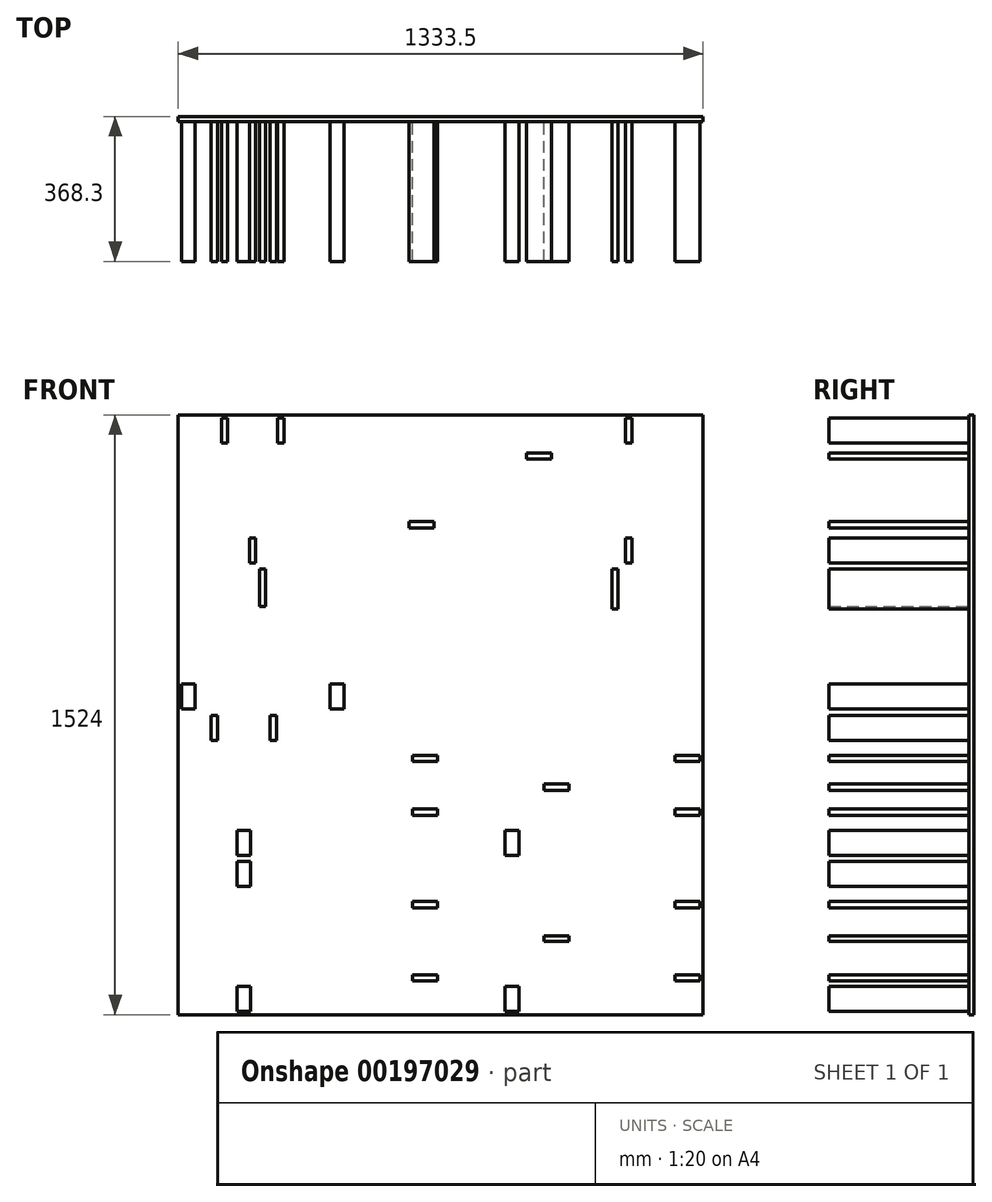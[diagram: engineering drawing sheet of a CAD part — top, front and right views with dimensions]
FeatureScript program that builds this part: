
annotation { "Feature Type Name" : "Feature", "Feature Type Description" : "" }
export const myFeature = defineFeature(function(context is Context, id is Id, definition is map)
    precondition{}
    {
        {
            var Q0;
            Q0=qCreatedBy(makeId("Front.planeOp"),FACE);
            var sketch = newSketch(context, id + "F0", { "sketchPlane" : qUnion([Q0])});
            skLineSegment(sketch, "E0.bottom", {"start": v(0, 0) * mm, "end": v(1333.5, 0) * mm});
            skLineSegment(sketch, "E0.top", {"start": v(0, 1524) * mm, "end": v(1333.5, 1524) * mm});
            skLineSegment(sketch, "E0.left", {"start": v(0, 0) * mm, "end": v(0, 1524) * mm});
            skLineSegment(sketch, "E0.right", {"start": v(1333.5, 0) * mm, "end": v(1333.5, 1524) * mm});
            skLineSegment(sketch, "E1.bottom", {"start": v(0, 1147.76) * mm, "end": v(1333.5, 1147.76) * mm, "construction": true});
            skLineSegment(sketch, "E1.top", {"start": v(0, 1131.89) * mm, "end": v(1333.5, 1131.89) * mm, "construction": true});
            skLineSegment(sketch, "E2.bottom", {"start": v(0, 776.29) * mm, "end": v(1333.5, 776.29) * mm, "construction": true});
            skLineSegment(sketch, "E2.top", {"start": v(0, 760.41) * mm, "end": v(1333.5, 760.41) * mm, "construction": true});
            skLineSegment(sketch, "E3.bottom", {"start": v(0, 404.81) * mm, "end": v(1333.5, 404.81) * mm, "construction": true});
            skLineSegment(sketch, "E3.top", {"start": v(0, 388.94) * mm, "end": v(1333.5, 388.94) * mm, "construction": true});
            skLineSegment(sketch, "E4.left", {"start": v(325.44, 776.29) * mm, "end": v(325.44, 0) * mm, "construction": true});
            skLineSegment(sketch, "E5.trimOffspring", {"start": v(341.31, 776.29) * mm, "end": v(341.31, 0) * mm, "construction": true});
            skLineSegment(sketch, "E6.trimOffspring", {"start": v(658.81, 776.29) * mm, "end": v(658.81, 0) * mm, "construction": true});
            skLineSegment(sketch, "E7.trimOffspring", {"start": v(674.69, 776.29) * mm, "end": v(674.69, 0) * mm, "construction": true});
            skLineSegment(sketch, "E8.trimOffspring", {"start": v(992.19, 776.29) * mm, "end": v(992.19, 0) * mm, "construction": true});
            skLineSegment(sketch, "E9.trimOffspring", {"start": v(1008.06, 776.29) * mm, "end": v(1008.06, 0) * mm, "construction": true});
            skLineSegment(sketch, "E10.bottom", {"start": v(7.94, 1516.06) * mm, "end": v(1325.56, 1516.06) * mm, "construction": true});
            skLineSegment(sketch, "E10.top", {"start": v(7.94, 7.94) * mm, "end": v(1325.56, 7.94) * mm, "construction": true});
            skLineSegment(sketch, "E10.left", {"start": v(7.94, 1516.06) * mm, "end": v(7.94, 7.94) * mm, "construction": true});
            skLineSegment(sketch, "E10.right", {"start": v(1325.56, 1516.06) * mm, "end": v(1325.56, 7.94) * mm, "construction": true});
            skLineSegment(sketch, "E11.bottom", {"start": v(595.31, 658.81) * mm, "end": v(658.81, 658.81) * mm});
            skLineSegment(sketch, "E11.top", {"start": v(595.31, 642.94) * mm, "end": v(658.81, 642.94) * mm});
            skLineSegment(sketch, "E11.left", {"start": v(595.31, 658.81) * mm, "end": v(595.31, 642.94) * mm});
            skLineSegment(sketch, "E11.right", {"start": v(658.81, 658.81) * mm, "end": v(658.81, 642.94) * mm});
            skLineSegment(sketch, "E12.bottom", {"start": v(896.94, 1131.89) * mm, "end": v(912.81, 1131.89) * mm});
            skLineSegment(sketch, "E12.top", {"start": v(896.94, 776.29) * mm, "end": v(912.81, 776.29) * mm});
            skLineSegment(sketch, "E12.left", {"start": v(896.94, 1131.89) * mm, "end": v(896.94, 776.29) * mm, "construction": true});
            skLineSegment(sketch, "E12.right", {"start": v(912.81, 1131.89) * mm, "end": v(912.81, 776.29) * mm, "construction": true});
            skLineSegment(sketch, "E13.bottom", {"start": v(436.56, 1131.89) * mm, "end": v(420.69, 1131.89) * mm});
            skLineSegment(sketch, "E13.top", {"start": v(436.56, 776.29) * mm, "end": v(420.69, 776.29) * mm});
            skLineSegment(sketch, "E13.left", {"start": v(436.56, 1131.89) * mm, "end": v(436.56, 776.29) * mm, "construction": true});
            skLineSegment(sketch, "E13.right", {"start": v(420.69, 1131.89) * mm, "end": v(420.69, 776.29) * mm, "construction": true});
            skLineSegment(sketch, "E14.bottom", {"start": v(206.37, 1131.89) * mm, "end": v(222.25, 1131.89) * mm});
            skLineSegment(sketch, "E14.top", {"start": v(206.37, 1036.64) * mm, "end": v(222.25, 1036.64) * mm});
            skLineSegment(sketch, "E14.left", {"start": v(206.38, 1131.89) * mm, "end": v(206.38, 1036.64) * mm});
            skLineSegment(sketch, "E14.right", {"start": v(222.25, 1131.89) * mm, "end": v(222.25, 1036.64) * mm});
            skLineSegment(sketch, "E15.bottom", {"start": v(369.89, 1516.06) * mm, "end": v(385.76, 1516.06) * mm});
            skLineSegment(sketch, "E15.top", {"start": v(369.89, 1147.76) * mm, "end": v(385.76, 1147.76) * mm});
            skLineSegment(sketch, "E15.left", {"start": v(369.89, 1516.06) * mm, "end": v(369.89, 1147.76) * mm, "construction": true});
            skLineSegment(sketch, "E15.right", {"start": v(385.76, 1516.06) * mm, "end": v(385.76, 1147.76) * mm, "construction": true});
            skLineSegment(sketch, "E16.bottom", {"start": v(1101.73, 1131.89) * mm, "end": v(1117.6, 1131.89) * mm});
            skLineSegment(sketch, "E16.top", {"start": v(1101.72, 1030.29) * mm, "end": v(1117.6, 1030.29) * mm});
            skLineSegment(sketch, "E16.left", {"start": v(1101.73, 1131.89) * mm, "end": v(1101.73, 1030.29) * mm});
            skLineSegment(sketch, "E16.right", {"start": v(1117.6, 1131.89) * mm, "end": v(1117.6, 1030.29) * mm});
            skLineSegment(sketch, "E17.bottom", {"start": v(149.23, 388.94) * mm, "end": v(184.15, 388.94) * mm});
            skLineSegment(sketch, "E17.top", {"start": v(149.23, 325.44) * mm, "end": v(184.15, 325.44) * mm});
            skLineSegment(sketch, "E17.left", {"start": v(149.23, 388.94) * mm, "end": v(149.23, 325.44) * mm});
            skLineSegment(sketch, "E17.right", {"start": v(184.15, 388.94) * mm, "end": v(184.15, 325.44) * mm});
            skLineSegment(sketch, "E18.bottom", {"start": v(595.31, 287.34) * mm, "end": v(658.81, 287.34) * mm});
            skLineSegment(sketch, "E18.top", {"start": v(595.31, 271.46) * mm, "end": v(658.81, 271.46) * mm});
            skLineSegment(sketch, "E18.left", {"start": v(595.31, 287.34) * mm, "end": v(595.31, 271.46) * mm});
            skLineSegment(sketch, "E18.right", {"start": v(658.81, 287.34) * mm, "end": v(658.81, 271.46) * mm});
            skLineSegment(sketch, "E19.bottom", {"start": v(149.23, 71.44) * mm, "end": v(184.15, 71.44) * mm});
            skLineSegment(sketch, "E19.top", {"start": v(149.23, 7.94) * mm, "end": v(184.15, 7.94) * mm});
            skLineSegment(sketch, "E19.left", {"start": v(149.23, 71.44) * mm, "end": v(149.23, 7.94) * mm});
            skLineSegment(sketch, "E19.right", {"start": v(184.15, 71.44) * mm, "end": v(184.15, 7.94) * mm});
            skLineSegment(sketch, "E20", {"start": v(166.69, 325.44) * mm, "end": v(166.69, 388.94) * mm, "construction": true});
            skPoint(sketch, "E21", {"position": v(166.69, 363.54) * mm});
            skLineSegment(sketch, "E22", {"start": v(166.69, 71.44) * mm, "end": v(166.69, 7.94) * mm, "construction": true});
            skPoint(sketch, "E23", {"position": v(166.69, 33.34) * mm});
            skLineSegment(sketch, "E24.bottom", {"start": v(595.31, 101.6) * mm, "end": v(658.81, 101.6) * mm});
            skLineSegment(sketch, "E24.top", {"start": v(595.31, 85.73) * mm, "end": v(658.81, 85.73) * mm});
            skLineSegment(sketch, "E24.left", {"start": v(595.31, 101.6) * mm, "end": v(595.31, 85.73) * mm});
            skLineSegment(sketch, "E24.right", {"start": v(658.81, 101.6) * mm, "end": v(658.81, 85.73) * mm});
            skLineSegment(sketch, "E25.bottom", {"start": v(992.19, 200.74) * mm, "end": v(928.69, 200.74) * mm});
            skLineSegment(sketch, "E25.top", {"start": v(992.19, 185.74) * mm, "end": v(928.69, 185.74) * mm});
            skLineSegment(sketch, "E25.left", {"start": v(992.19, 200.74) * mm, "end": v(992.19, 185.74) * mm});
            skLineSegment(sketch, "E25.right", {"start": v(928.69, 200.74) * mm, "end": v(928.69, 185.74) * mm});
            skLineSegment(sketch, "E26.bottom", {"start": v(865.19, 7.94) * mm, "end": v(830.26, 7.94) * mm});
            skLineSegment(sketch, "E26.top", {"start": v(865.19, 71.44) * mm, "end": v(830.26, 71.44) * mm});
            skLineSegment(sketch, "E26.left", {"start": v(830.26, 7.94) * mm, "end": v(830.26, 71.44) * mm});
            skLineSegment(sketch, "E26.right", {"start": v(865.19, 7.94) * mm, "end": v(865.19, 71.44) * mm});
            skLineSegment(sketch, "E27.bottom", {"start": v(1262.06, 271.46) * mm, "end": v(1325.56, 271.46) * mm});
            skLineSegment(sketch, "E27.top", {"start": v(1262.06, 287.34) * mm, "end": v(1325.56, 287.34) * mm});
            skLineSegment(sketch, "E27.left", {"start": v(1262.06, 271.46) * mm, "end": v(1262.06, 287.34) * mm});
            skLineSegment(sketch, "E27.right", {"start": v(1325.56, 271.46) * mm, "end": v(1325.56, 287.34) * mm});
            skLineSegment(sketch, "E28.bottom", {"start": v(1262.06, 101.6) * mm, "end": v(1325.56, 101.6) * mm});
            skLineSegment(sketch, "E28.top", {"start": v(1262.06, 85.73) * mm, "end": v(1325.56, 85.73) * mm});
            skLineSegment(sketch, "E28.left", {"start": v(1262.06, 101.6) * mm, "end": v(1262.06, 85.73) * mm});
            skLineSegment(sketch, "E28.right", {"start": v(1325.56, 101.6) * mm, "end": v(1325.56, 85.73) * mm});
            skLineSegment(sketch, "E29.bottom", {"start": v(84.14, 760.41) * mm, "end": v(100.01, 760.41) * mm});
            skLineSegment(sketch, "E29.top", {"start": v(84.14, 696.91) * mm, "end": v(100.01, 696.91) * mm});
            skLineSegment(sketch, "E29.left", {"start": v(84.14, 760.41) * mm, "end": v(84.14, 696.91) * mm});
            skLineSegment(sketch, "E29.right", {"start": v(100.01, 760.41) * mm, "end": v(100.01, 696.91) * mm});
            skLineSegment(sketch, "E30.bottom", {"start": v(149.22, 404.81) * mm, "end": v(184.15, 404.81) * mm});
            skLineSegment(sketch, "E30.top", {"start": v(149.22, 468.31) * mm, "end": v(184.15, 468.31) * mm});
            skLineSegment(sketch, "E30.left", {"start": v(149.22, 404.81) * mm, "end": v(149.22, 468.31) * mm});
            skLineSegment(sketch, "E30.right", {"start": v(184.15, 404.81) * mm, "end": v(184.15, 468.31) * mm});
            skLineSegment(sketch, "E31.bottom", {"start": v(233.36, 760.41) * mm, "end": v(249.24, 760.41) * mm});
            skLineSegment(sketch, "E31.top", {"start": v(233.36, 696.91) * mm, "end": v(249.24, 696.91) * mm});
            skLineSegment(sketch, "E31.left", {"start": v(233.36, 760.41) * mm, "end": v(233.36, 696.91) * mm});
            skLineSegment(sketch, "E31.right", {"start": v(249.24, 760.41) * mm, "end": v(249.24, 696.91) * mm});
            skLineSegment(sketch, "E32", {"start": v(166.69, 468.31) * mm, "end": v(166.69, 404.81) * mm, "construction": true});
            skLineSegment(sketch, "E33.bottom", {"start": v(595.31, 522.29) * mm, "end": v(658.81, 522.29) * mm});
            skLineSegment(sketch, "E33.top", {"start": v(595.31, 506.41) * mm, "end": v(658.81, 506.41) * mm});
            skLineSegment(sketch, "E33.left", {"start": v(595.31, 522.29) * mm, "end": v(595.31, 506.41) * mm});
            skLineSegment(sketch, "E33.right", {"start": v(658.81, 522.29) * mm, "end": v(658.81, 506.41) * mm});
            skLineSegment(sketch, "E34.bottom", {"start": v(992.19, 569.91) * mm, "end": v(928.69, 569.91) * mm});
            skLineSegment(sketch, "E34.top", {"start": v(992.19, 585.79) * mm, "end": v(928.69, 585.79) * mm});
            skLineSegment(sketch, "E34.left", {"start": v(992.19, 569.91) * mm, "end": v(992.19, 585.79) * mm});
            skLineSegment(sketch, "E34.right", {"start": v(928.69, 569.91) * mm, "end": v(928.69, 585.79) * mm});
            skLineSegment(sketch, "E35.bottom", {"start": v(865.19, 404.81) * mm, "end": v(830.26, 404.81) * mm});
            skLineSegment(sketch, "E35.top", {"start": v(865.19, 468.31) * mm, "end": v(830.26, 468.31) * mm});
            skLineSegment(sketch, "E35.left", {"start": v(865.19, 404.81) * mm, "end": v(865.19, 468.31) * mm});
            skLineSegment(sketch, "E35.right", {"start": v(830.26, 404.81) * mm, "end": v(830.26, 468.31) * mm});
            skLineSegment(sketch, "E36.bottom", {"start": v(1262.06, 658.81) * mm, "end": v(1325.56, 658.81) * mm});
            skLineSegment(sketch, "E36.top", {"start": v(1262.06, 642.94) * mm, "end": v(1325.56, 642.94) * mm});
            skLineSegment(sketch, "E36.left", {"start": v(1262.06, 658.81) * mm, "end": v(1262.06, 642.94) * mm});
            skLineSegment(sketch, "E36.right", {"start": v(1325.56, 658.81) * mm, "end": v(1325.56, 642.94) * mm});
            skLineSegment(sketch, "E37.bottom", {"start": v(1262.06, 522.29) * mm, "end": v(1325.56, 522.29) * mm});
            skLineSegment(sketch, "E37.top", {"start": v(1262.06, 506.41) * mm, "end": v(1325.56, 506.41) * mm});
            skLineSegment(sketch, "E37.left", {"start": v(1262.06, 522.29) * mm, "end": v(1262.06, 506.41) * mm});
            skLineSegment(sketch, "E37.right", {"start": v(1325.56, 522.29) * mm, "end": v(1325.56, 506.41) * mm});
            skLineSegment(sketch, "E38.bottom", {"start": v(7.94, 839.79) * mm, "end": v(42.86, 839.79) * mm});
            skLineSegment(sketch, "E38.top", {"start": v(7.94, 776.29) * mm, "end": v(42.86, 776.29) * mm});
            skLineSegment(sketch, "E38.left", {"start": v(7.94, 839.79) * mm, "end": v(7.94, 776.29) * mm});
            skLineSegment(sketch, "E38.right", {"start": v(42.86, 839.79) * mm, "end": v(42.86, 776.29) * mm});
            skLineSegment(sketch, "E39.bottom", {"start": v(420.69, 776.29) * mm, "end": v(385.76, 776.29) * mm});
            skLineSegment(sketch, "E39.top", {"start": v(420.69, 839.79) * mm, "end": v(385.76, 839.79) * mm});
            skLineSegment(sketch, "E39.left", {"start": v(420.69, 776.29) * mm, "end": v(420.69, 839.79) * mm});
            skLineSegment(sketch, "E39.right", {"start": v(385.76, 776.29) * mm, "end": v(385.76, 839.79) * mm});
            skLineSegment(sketch, "E40.bottom", {"start": v(569.91, 1516.06) * mm, "end": v(585.79, 1516.06) * mm});
            skLineSegment(sketch, "E40.top", {"start": v(569.91, 1147.76) * mm, "end": v(585.79, 1147.76) * mm});
            skLineSegment(sketch, "E40.left", {"start": v(569.91, 1516.06) * mm, "end": v(569.91, 1147.76) * mm, "construction": true});
            skLineSegment(sketch, "E40.right", {"start": v(585.79, 1516.06) * mm, "end": v(585.79, 1147.76) * mm, "construction": true});
            skLineSegment(sketch, "E41.bottom", {"start": v(947.74, 1516.06) * mm, "end": v(963.61, 1516.06) * mm});
            skLineSegment(sketch, "E41.top", {"start": v(947.74, 1147.76) * mm, "end": v(963.61, 1147.76) * mm});
            skLineSegment(sketch, "E41.left", {"start": v(947.74, 1516.06) * mm, "end": v(947.74, 1147.76) * mm, "construction": true});
            skLineSegment(sketch, "E41.right", {"start": v(963.61, 1516.06) * mm, "end": v(963.61, 1147.76) * mm, "construction": true});
            skLineSegment(sketch, "E42.bottom", {"start": v(109.54, 1516.06) * mm, "end": v(125.41, 1516.06) * mm});
            skLineSegment(sketch, "E42.top", {"start": v(109.54, 1452.56) * mm, "end": v(125.41, 1452.56) * mm});
            skLineSegment(sketch, "E42.left", {"start": v(109.54, 1516.06) * mm, "end": v(109.54, 1452.56) * mm});
            skLineSegment(sketch, "E42.right", {"start": v(125.41, 1516.06) * mm, "end": v(125.41, 1452.56) * mm});
            skLineSegment(sketch, "E43.bottom", {"start": v(252.41, 1516.06) * mm, "end": v(268.29, 1516.06) * mm});
            skLineSegment(sketch, "E43.top", {"start": v(252.41, 1452.56) * mm, "end": v(268.29, 1452.56) * mm});
            skLineSegment(sketch, "E43.left", {"start": v(252.41, 1516.06) * mm, "end": v(252.41, 1452.56) * mm});
            skLineSegment(sketch, "E43.right", {"start": v(268.29, 1516.06) * mm, "end": v(268.29, 1452.56) * mm});
            skLineSegment(sketch, "E44.bottom", {"start": v(180.98, 1211.26) * mm, "end": v(196.85, 1211.26) * mm});
            skLineSegment(sketch, "E44.top", {"start": v(180.98, 1147.76) * mm, "end": v(196.85, 1147.76) * mm});
            skLineSegment(sketch, "E44.left", {"start": v(180.98, 1211.26) * mm, "end": v(180.98, 1147.76) * mm});
            skLineSegment(sketch, "E44.right", {"start": v(196.85, 1211.26) * mm, "end": v(196.85, 1147.76) * mm});
            skLineSegment(sketch, "E45", {"start": v(188.91, 1147.76) * mm, "end": v(188.91, 1211.26) * mm, "construction": true});
            skLineSegment(sketch, "E46.bottom", {"start": v(385.76, 1414.46) * mm, "end": v(569.91, 1414.46) * mm});
            skLineSegment(sketch, "E46.top", {"start": v(385.76, 1398.59) * mm, "end": v(569.91, 1398.59) * mm});
            skLineSegment(sketch, "E46.left", {"start": v(385.76, 1414.46) * mm, "end": v(385.76, 1398.59) * mm});
            skLineSegment(sketch, "E46.right", {"start": v(569.91, 1414.46) * mm, "end": v(569.91, 1398.59) * mm});
            skLineSegment(sketch, "E47.bottom", {"start": v(884.24, 1427.16) * mm, "end": v(947.74, 1427.16) * mm});
            skLineSegment(sketch, "E47.top", {"start": v(884.24, 1411.29) * mm, "end": v(947.74, 1411.29) * mm});
            skLineSegment(sketch, "E47.left", {"start": v(884.24, 1427.16) * mm, "end": v(884.24, 1411.29) * mm});
            skLineSegment(sketch, "E47.right", {"start": v(947.74, 1427.16) * mm, "end": v(947.74, 1411.29) * mm});
            skLineSegment(sketch, "E48.bottom", {"start": v(585.79, 1252.54) * mm, "end": v(649.29, 1252.54) * mm});
            skLineSegment(sketch, "E48.top", {"start": v(585.79, 1236.66) * mm, "end": v(649.29, 1236.66) * mm});
            skLineSegment(sketch, "E48.left", {"start": v(585.79, 1252.54) * mm, "end": v(585.79, 1236.66) * mm});
            skLineSegment(sketch, "E48.right", {"start": v(649.29, 1252.54) * mm, "end": v(649.29, 1236.66) * mm});
            skLineSegment(sketch, "E49.bottom", {"start": v(1136.65, 1211.26) * mm, "end": v(1152.53, 1211.26) * mm});
            skLineSegment(sketch, "E49.top", {"start": v(1136.65, 1147.76) * mm, "end": v(1152.53, 1147.76) * mm});
            skLineSegment(sketch, "E49.left", {"start": v(1136.65, 1211.26) * mm, "end": v(1136.65, 1147.76) * mm});
            skLineSegment(sketch, "E49.right", {"start": v(1152.53, 1211.26) * mm, "end": v(1152.53, 1147.76) * mm});
            skLineSegment(sketch, "E50", {"start": v(1144.59, 1147.76) * mm, "end": v(1144.59, 1211.26) * mm, "construction": true});
            skLineSegment(sketch, "E51.bottom", {"start": v(1152.53, 1452.56) * mm, "end": v(1136.65, 1452.56) * mm});
            skLineSegment(sketch, "E51.top", {"start": v(1152.53, 1516.06) * mm, "end": v(1136.65, 1516.06) * mm});
            skLineSegment(sketch, "E51.left", {"start": v(1152.53, 1452.56) * mm, "end": v(1152.53, 1516.06) * mm});
            skLineSegment(sketch, "E51.right", {"start": v(1136.65, 1452.56) * mm, "end": v(1136.65, 1516.06) * mm});
            skSolve(sketch);
        }
        {
            var Q0;
            Q0=makeQuery(id+"F0.imprint","IMPRINT",FACE,{"disambiguationData":[TD([[makeQuery(id+"F0.imprint","IMPRINT",EDGE,{"derivedFrom":sQuery(id+"F0.wireOp",EDGE,"E19.bottom")}),-1.0]])]});
            var Q1;
            Q1=makeQuery(id+"F0.imprint","IMPRINT",FACE,{"disambiguationData":[TD([[makeQuery(id+"F0.imprint","IMPRINT",EDGE,{"derivedFrom":sQuery(id+"F0.wireOp",EDGE,"E24.bottom")}),-1.0]])]});
            var Q2;
            Q2=makeQuery(id+"F0.imprint","IMPRINT",FACE,{"disambiguationData":[TD([[makeQuery(id+"F0.imprint","IMPRINT",EDGE,{"derivedFrom":sQuery(id+"F0.wireOp",EDGE,"E18.bottom")}),-1.0]])]});
            var Q3;
            Q3=makeQuery(id+"F0.imprint","IMPRINT",FACE,{"disambiguationData":[TD([[makeQuery(id+"F0.imprint","IMPRINT",EDGE,{"derivedFrom":sQuery(id+"F0.wireOp",EDGE,"E26.bottom")}),-1.0]])]});
            var Q4;
            Q4=makeQuery(id+"F0.imprint","IMPRINT",FACE,{"disambiguationData":[TD([[makeQuery(id+"F0.imprint","IMPRINT",EDGE,{"derivedFrom":sQuery(id+"F0.wireOp",EDGE,"E25.bottom")}),1.0]])]});
            var Q5;
            Q5=makeQuery(id+"F0.imprint","IMPRINT",FACE,{"disambiguationData":[TD([[makeQuery(id+"F0.imprint","IMPRINT",EDGE,{"derivedFrom":sQuery(id+"F0.wireOp",EDGE,"E28.bottom")}),-1.0]])]});
            var Q6;
            Q6=makeQuery(id+"F0.imprint","IMPRINT",FACE,{"disambiguationData":[TD([[makeQuery(id+"F0.imprint","IMPRINT",EDGE,{"derivedFrom":sQuery(id+"F0.wireOp",EDGE,"E27.bottom")}),1.0]])]});
            var Q7;
            Q7=makeQuery(id+"F0.imprint","IMPRINT",FACE,{"disambiguationData":[TD([[makeQuery(id+"F0.imprint","IMPRINT",EDGE,{"derivedFrom":sQuery(id+"F0.wireOp",EDGE,"E17.bottom")}),-1.0]])]});
            var Q8;
            Q8=makeQuery(id+"F0.imprint","IMPRINT",FACE,{"disambiguationData":[TD([[makeQuery(id+"F0.imprint","IMPRINT",EDGE,{"derivedFrom":sQuery(id+"F0.wireOp",EDGE,"E30.bottom")}),1.0]])]});
            var Q9;
            Q9=makeQuery(id+"F0.imprint","IMPRINT",FACE,{"disambiguationData":[TD([[makeQuery(id+"F0.imprint","IMPRINT",EDGE,{"derivedFrom":sQuery(id+"F0.wireOp",EDGE,"E33.bottom")}),-1.0]])]});
            var Q10;
            Q10=makeQuery(id+"F0.imprint","IMPRINT",FACE,{"disambiguationData":[TD([[makeQuery(id+"F0.imprint","IMPRINT",EDGE,{"derivedFrom":sQuery(id+"F0.wireOp",EDGE,"E35.bottom")}),-1.0]])]});
            var Q11;
            Q11=makeQuery(id+"F0.imprint","IMPRINT",FACE,{"disambiguationData":[TD([[makeQuery(id+"F0.imprint","IMPRINT",EDGE,{"derivedFrom":sQuery(id+"F0.wireOp",EDGE,"E34.bottom")}),-1.0]])]});
            var Q12;
            Q12=makeQuery(id+"F0.imprint","IMPRINT",FACE,{"disambiguationData":[TD([[makeQuery(id+"F0.imprint","IMPRINT",EDGE,{"derivedFrom":sQuery(id+"F0.wireOp",EDGE,"E37.bottom")}),-1.0]])]});
            var Q13;
            Q13=makeQuery(id+"F0.imprint","IMPRINT",FACE,{"disambiguationData":[TD([[makeQuery(id+"F0.imprint","IMPRINT",EDGE,{"derivedFrom":sQuery(id+"F0.wireOp",EDGE,"E36.bottom")}),-1.0]])]});
            var Q14;
            Q14=makeQuery(id+"F0.imprint","IMPRINT",FACE,{"disambiguationData":[TD([[makeQuery(id+"F0.imprint","IMPRINT",EDGE,{"derivedFrom":sQuery(id+"F0.wireOp",EDGE,"E11.bottom")}),-1.0]])]});
            var Q15;
            Q15=makeQuery(id+"F0.imprint","IMPRINT",FACE,{"disambiguationData":[TD([[makeQuery(id+"F0.imprint","IMPRINT",EDGE,{"derivedFrom":sQuery(id+"F0.wireOp",EDGE,"E29.bottom")}),-1.0]])]});
            var Q16;
            Q16=makeQuery(id+"F0.imprint","IMPRINT",FACE,{"disambiguationData":[TD([[makeQuery(id+"F0.imprint","IMPRINT",EDGE,{"derivedFrom":sQuery(id+"F0.wireOp",EDGE,"E31.bottom")}),-1.0]])]});
            var Q17;
            Q17=makeQuery(id+"F0.imprint","IMPRINT",FACE,{"disambiguationData":[TD([[makeQuery(id+"F0.imprint","IMPRINT",EDGE,{"derivedFrom":sQuery(id+"F0.wireOp",EDGE,"E39.bottom")}),-1.0]])]});
            var Q18;
            Q18=makeQuery(id+"F0.imprint","IMPRINT",FACE,{"disambiguationData":[TD([[makeQuery(id+"F0.imprint","IMPRINT",EDGE,{"derivedFrom":sQuery(id+"F0.wireOp",EDGE,"E44.bottom")}),-1.0]])]});
            var Q19;
            Q19=makeQuery(id+"F0.imprint","IMPRINT",FACE,{"disambiguationData":[TD([[makeQuery(id+"F0.imprint","IMPRINT",EDGE,{"derivedFrom":sQuery(id+"F0.wireOp",EDGE,"E42.bottom")}),-1.0]])]});
            var Q20;
            Q20=makeQuery(id+"F0.imprint","IMPRINT",FACE,{"disambiguationData":[TD([[makeQuery(id+"F0.imprint","IMPRINT",EDGE,{"derivedFrom":sQuery(id+"F0.wireOp",EDGE,"E43.bottom")}),-1.0]])]});
            var Q21;
            Q21=makeQuery(id+"F0.imprint","IMPRINT",FACE,{"disambiguationData":[TD([[makeQuery(id+"F0.imprint","IMPRINT",EDGE,{"derivedFrom":sQuery(id+"F0.wireOp",EDGE,"E48.bottom")}),-1.0]])]});
            var Q22;
            Q22=makeQuery(id+"F0.imprint","IMPRINT",FACE,{"disambiguationData":[TD([[makeQuery(id+"F0.imprint","IMPRINT",EDGE,{"derivedFrom":sQuery(id+"F0.wireOp",EDGE,"E47.bottom")}),-1.0]])]});
            var Q23;
            Q23=makeQuery(id+"F0.imprint","IMPRINT",FACE,{"disambiguationData":[TD([[makeQuery(id+"F0.imprint","IMPRINT",EDGE,{"derivedFrom":sQuery(id+"F0.wireOp",EDGE,"E51.bottom")}),-1.0]])]});
            var Q24;
            Q24=makeQuery(id+"F0.imprint","IMPRINT",FACE,{"disambiguationData":[TD([[makeQuery(id+"F0.imprint","IMPRINT",EDGE,{"derivedFrom":sQuery(id+"F0.wireOp",EDGE,"E49.bottom")}),-1.0]])]});
            var Q25;
            Q25=makeQuery(id+"F0.imprint","IMPRINT",FACE,{"disambiguationData":[TD([[makeQuery(id+"F0.imprint","IMPRINT",EDGE,{"derivedFrom":sQuery(id+"F0.wireOp",EDGE,"E38.bottom")}),-1.0]])]});
            var Q26;
            Q26=makeQuery(id+"F0.imprint","IMPRINT",FACE,{"disambiguationData":[TD([[makeQuery(id+"F0.imprint","IMPRINT",EDGE,{"derivedFrom":sQuery(id+"F0.wireOp",EDGE,"E16.bottom")}),-1.0]])]});
            var Q27;
            Q27=makeQuery(id+"F0.imprint","IMPRINT",FACE,{"disambiguationData":[TD([[makeQuery(id+"F0.imprint","IMPRINT",EDGE,{"derivedFrom":sQuery(id+"F0.wireOp",EDGE,"E14.bottom")}),-1.0]])]});
            var Q28;
            Q28=makeQuery(id+"F0.imprint","IMPRINT",FACE,{"disambiguationData":[TD([[makeQuery(id+"F0.imprint","IMPRINT",EDGE,{"derivedFrom":sQuery(id+"F0.wireOp",EDGE,"E46.bottom")}),-1.0]])]});
            var Q29;
            Q29=makeQuery(id+"F0.imprint","IMPRINT",FACE,{"disambiguationData":[TD([[makeQuery(id+"F0.imprint","IMPRINT",EDGE,{"derivedFrom":sQuery(id+"F0.wireOp",EDGE,"E0.bottom")}),1.0]])]});
            extrude(context, id + "F1", {"entities" : qUnion([Q0, Q1, Q2, Q3, Q4, Q5, Q6, Q7, Q8, Q9, Q10, Q11, Q12, Q13, Q14, Q15, Q16, Q17, Q18, Q19, Q20, Q21, Q22, Q23, Q24, Q25, Q26, Q27, Q28, Q29]), "depth" : 12.7 * mm});
        }
        {
            var Q0;
            Q0=makeQuery(id+"F0.imprint","IMPRINT",FACE,{"disambiguationData":[TD([[makeQuery(id+"F0.imprint","IMPRINT",EDGE,{"derivedFrom":sQuery(id+"F0.wireOp",EDGE,"E51.bottom")}),-1.0]])]});
            var Q1;
            Q1=makeQuery(id+"F0.imprint","IMPRINT",FACE,{"disambiguationData":[TD([[makeQuery(id+"F0.imprint","IMPRINT",EDGE,{"derivedFrom":sQuery(id+"F0.wireOp",EDGE,"E49.bottom")}),-1.0]])]});
            var Q2;
            Q2=makeQuery(id+"F0.imprint","IMPRINT",FACE,{"disambiguationData":[TD([[makeQuery(id+"F0.imprint","IMPRINT",EDGE,{"derivedFrom":sQuery(id+"F0.wireOp",EDGE,"E16.bottom")}),-1.0]])]});
            var Q3;
            Q3=makeQuery(id+"F0.imprint","IMPRINT",FACE,{"disambiguationData":[TD([[makeQuery(id+"F0.imprint","IMPRINT",EDGE,{"derivedFrom":sQuery(id+"F0.wireOp",EDGE,"E47.bottom")}),-1.0]])]});
            var Q4;
            Q4=makeQuery(id+"F0.imprint","IMPRINT",FACE,{"disambiguationData":[TD([[makeQuery(id+"F0.imprint","IMPRINT",EDGE,{"derivedFrom":sQuery(id+"F0.wireOp",EDGE,"E48.bottom")}),-1.0]])]});
            var Q5;
            Q5=makeQuery(id+"F0.imprint","IMPRINT",FACE,{"disambiguationData":[TD([[makeQuery(id+"F0.imprint","IMPRINT",EDGE,{"derivedFrom":sQuery(id+"F0.wireOp",EDGE,"E44.bottom")}),-1.0]])]});
            var Q6;
            Q6=makeQuery(id+"F0.imprint","IMPRINT",FACE,{"disambiguationData":[TD([[makeQuery(id+"F0.imprint","IMPRINT",EDGE,{"derivedFrom":sQuery(id+"F0.wireOp",EDGE,"E43.bottom")}),-1.0]])]});
            var Q7;
            Q7=makeQuery(id+"F0.imprint","IMPRINT",FACE,{"disambiguationData":[TD([[makeQuery(id+"F0.imprint","IMPRINT",EDGE,{"derivedFrom":sQuery(id+"F0.wireOp",EDGE,"E42.bottom")}),-1.0]])]});
            var Q8;
            Q8=makeQuery(id+"F0.imprint","IMPRINT",FACE,{"disambiguationData":[TD([[makeQuery(id+"F0.imprint","IMPRINT",EDGE,{"derivedFrom":sQuery(id+"F0.wireOp",EDGE,"E38.bottom")}),-1.0]])]});
            var Q9;
            Q9=makeQuery(id+"F0.imprint","IMPRINT",FACE,{"disambiguationData":[TD([[makeQuery(id+"F0.imprint","IMPRINT",EDGE,{"derivedFrom":sQuery(id+"F0.wireOp",EDGE,"E14.bottom")}),-1.0]])]});
            var Q10;
            Q10=makeQuery(id+"F0.imprint","IMPRINT",FACE,{"disambiguationData":[TD([[makeQuery(id+"F0.imprint","IMPRINT",EDGE,{"derivedFrom":sQuery(id+"F0.wireOp",EDGE,"E39.bottom")}),-1.0]])]});
            var Q11;
            Q11=makeQuery(id+"F0.imprint","IMPRINT",FACE,{"disambiguationData":[TD([[makeQuery(id+"F0.imprint","IMPRINT",EDGE,{"derivedFrom":sQuery(id+"F0.wireOp",EDGE,"E31.bottom")}),-1.0]])]});
            var Q12;
            Q12=makeQuery(id+"F0.imprint","IMPRINT",FACE,{"disambiguationData":[TD([[makeQuery(id+"F0.imprint","IMPRINT",EDGE,{"derivedFrom":sQuery(id+"F0.wireOp",EDGE,"E29.bottom")}),-1.0]])]});
            var Q13;
            Q13=makeQuery(id+"F0.imprint","IMPRINT",FACE,{"disambiguationData":[TD([[makeQuery(id+"F0.imprint","IMPRINT",EDGE,{"derivedFrom":sQuery(id+"F0.wireOp",EDGE,"E30.bottom")}),1.0]])]});
            var Q14;
            Q14=makeQuery(id+"F0.imprint","IMPRINT",FACE,{"disambiguationData":[TD([[makeQuery(id+"F0.imprint","IMPRINT",EDGE,{"derivedFrom":sQuery(id+"F0.wireOp",EDGE,"E33.bottom")}),-1.0]])]});
            var Q15;
            Q15=makeQuery(id+"F0.imprint","IMPRINT",FACE,{"disambiguationData":[TD([[makeQuery(id+"F0.imprint","IMPRINT",EDGE,{"derivedFrom":sQuery(id+"F0.wireOp",EDGE,"E11.bottom")}),-1.0]])]});
            var Q16;
            Q16=makeQuery(id+"F0.imprint","IMPRINT",FACE,{"disambiguationData":[TD([[makeQuery(id+"F0.imprint","IMPRINT",EDGE,{"derivedFrom":sQuery(id+"F0.wireOp",EDGE,"E34.bottom")}),-1.0]])]});
            var Q17;
            Q17=makeQuery(id+"F0.imprint","IMPRINT",FACE,{"disambiguationData":[TD([[makeQuery(id+"F0.imprint","IMPRINT",EDGE,{"derivedFrom":sQuery(id+"F0.wireOp",EDGE,"E35.bottom")}),-1.0]])]});
            var Q18;
            Q18=makeQuery(id+"F0.imprint","IMPRINT",FACE,{"disambiguationData":[TD([[makeQuery(id+"F0.imprint","IMPRINT",EDGE,{"derivedFrom":sQuery(id+"F0.wireOp",EDGE,"E37.bottom")}),-1.0]])]});
            var Q19;
            Q19=makeQuery(id+"F0.imprint","IMPRINT",FACE,{"disambiguationData":[TD([[makeQuery(id+"F0.imprint","IMPRINT",EDGE,{"derivedFrom":sQuery(id+"F0.wireOp",EDGE,"E36.bottom")}),-1.0]])]});
            var Q20;
            Q20=makeQuery(id+"F0.imprint","IMPRINT",FACE,{"disambiguationData":[TD([[makeQuery(id+"F0.imprint","IMPRINT",EDGE,{"derivedFrom":sQuery(id+"F0.wireOp",EDGE,"E28.bottom")}),-1.0]])]});
            var Q21;
            Q21=makeQuery(id+"F0.imprint","IMPRINT",FACE,{"disambiguationData":[TD([[makeQuery(id+"F0.imprint","IMPRINT",EDGE,{"derivedFrom":sQuery(id+"F0.wireOp",EDGE,"E27.bottom")}),1.0]])]});
            var Q22;
            Q22=makeQuery(id+"F0.imprint","IMPRINT",FACE,{"disambiguationData":[TD([[makeQuery(id+"F0.imprint","IMPRINT",EDGE,{"derivedFrom":sQuery(id+"F0.wireOp",EDGE,"E25.bottom")}),1.0]])]});
            var Q23;
            Q23=makeQuery(id+"F0.imprint","IMPRINT",FACE,{"disambiguationData":[TD([[makeQuery(id+"F0.imprint","IMPRINT",EDGE,{"derivedFrom":sQuery(id+"F0.wireOp",EDGE,"E26.bottom")}),-1.0]])]});
            var Q24;
            Q24=makeQuery(id+"F0.imprint","IMPRINT",FACE,{"disambiguationData":[TD([[makeQuery(id+"F0.imprint","IMPRINT",EDGE,{"derivedFrom":sQuery(id+"F0.wireOp",EDGE,"E24.bottom")}),-1.0]])]});
            var Q25;
            Q25=makeQuery(id+"F0.imprint","IMPRINT",FACE,{"disambiguationData":[TD([[makeQuery(id+"F0.imprint","IMPRINT",EDGE,{"derivedFrom":sQuery(id+"F0.wireOp",EDGE,"E18.bottom")}),-1.0]])]});
            var Q26;
            Q26=makeQuery(id+"F0.imprint","IMPRINT",FACE,{"disambiguationData":[TD([[makeQuery(id+"F0.imprint","IMPRINT",EDGE,{"derivedFrom":sQuery(id+"F0.wireOp",EDGE,"E19.bottom")}),-1.0]])]});
            var Q27;
            Q27=makeQuery(id+"F0.imprint","IMPRINT",FACE,{"disambiguationData":[TD([[makeQuery(id+"F0.imprint","IMPRINT",EDGE,{"derivedFrom":sQuery(id+"F0.wireOp",EDGE,"E17.bottom")}),-1.0]])]});
            extrude(context, id + "F2", {"entities" : qUnion([Q0, Q1, Q2, Q3, Q4, Q5, Q6, Q7, Q8, Q9, Q10, Q11, Q12, Q13, Q14, Q15, Q16, Q17, Q18, Q19, Q20, Q21, Q22, Q23, Q24, Q25, Q26, Q27]), "depth" : 368.3 * mm, "hasSecondDirection" : true, "secondDirectionOppositeDirection" : false, "secondDirectionDepth" : 12.7 * mm});
        }
    });
